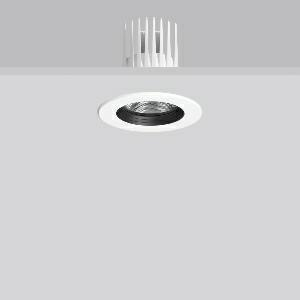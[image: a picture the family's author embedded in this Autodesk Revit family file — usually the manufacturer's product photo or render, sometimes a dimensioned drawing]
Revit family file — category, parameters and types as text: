
# Revit family: heledon_mini_e_901750_002_2_76_815f
name_source: partatom
category: Lighting Fixtures
units: mm (PartAtom-declared; Revit-internal decimal feet)

## family parameters
Cut with Voids When Loaded = No
Host = Face
Light Source = No
Part Type = Normal
Room Calculation Point = No
Round Connector Dimension = Use Diameter
Shared = No

## types (1)
- HELEDON mini E (1 x LED Modul 927, 3500 lm, 2700)
    Apparent Load = 29 VA
    Approval mark = CE
    CIE Flux Codes = 95 99 100 100 100
    Color Rendering = 92
    Color Temperature = 2700
    Default Elevation = 1800 mm
    Description = Series: HELEDON mini
Round recessed downlight. Housing: die-cast aluminium, powder-coated. Black plastic ring and recessed LED to prevent glare from the side. Optical assembly with reflector made of MIRO-Silver with 98% total light reflection for outstanding efficiency - can be changed without tools. Best colour rendering index Ra>90. Suitable for Recessed ceiling mounting. Installation without tools thanks to spring fastening system. Including separate LED converter with connecting cable 600 mm.High quality converter without flickering and stroboscopic effect. Through-wiring box (5 pole) available as accessory. The following accessories can be mounted without use of tools: interchangeable lenses, decorative glasses, honeycomb louvre, clear and frosted diffusers, white interchangeable plastic ring. 
Colour: traffic white, matt (RAL 9016)
Diameter: 124 mm
Height: 3 mm
Cut-out diameter: 114 mm
Recess height: 170 mm
Luminaire: recess height: 120 mm
Lamp: LED
Socket: without socket
Colour temperature: 2700K
Colour rendering index (CRI): 92
System power: 29 W
Rated luminous flux: 3500 lm
Luminous efficiency: 121 lm/W
Control gear: Converter, dimmable, DALI
Protection class: II
Type of protection: IP 20
    Height = 0 mm  [stored 0 ft]
    Lamp = 1 x LED Modul 927
    Lamp Light Flux = 3500 lm
    Lamp count = 1
    Length = 124 mm  [stored 0.406824 ft]
    Lifetime = 50000 h
    Luminous efficacy = 121 lm/W
    Manufacturer = RZB
    ModVariant = No
    Model = 901750.002.2.76
    Mounting Place = Ceiling
    Mounting Type = Recessed
    Number of Poles = 1
    OnlyDefault = Yes
    Power Factor = 1
    Product Name = HELEDON mini E
    Product group = Recessed downlights
    ProductGroupID = 402
    Protection Class = Protection class II
    Protection Degree = IP 20
    RLX_Detail_Level = 1
    RLX_Emergency_Light_Flux = 0 lm
    RLX_Emergency_Type = 0
    RLX_Emergency_Type_DB = No
    RlxData = <blob elided: 127453 chars, md5=96f630ba>
    Socket = socket
    Standby Power = 0 W
    System Light Flux = 3500 lm
    System Power = 29 W
    Type Comments = Product without accessories
    Type Image = 901657.002.jpg
    URL = http://relux.com
    VarID = ---
    Voltage = 230 V
    Voltage Range = 220-240 V
    Weight = 0.00 kg
    Width = 0 mm  [stored 0 ft]

note: [stored X ft] marks values corroborated as IEEE doubles in the binary element streams (Revit-internal decimal feet)

## geometry (parser evidence)
native form markers: Blend x4, Sweep x11
no freeform markers — native parametric forms only
